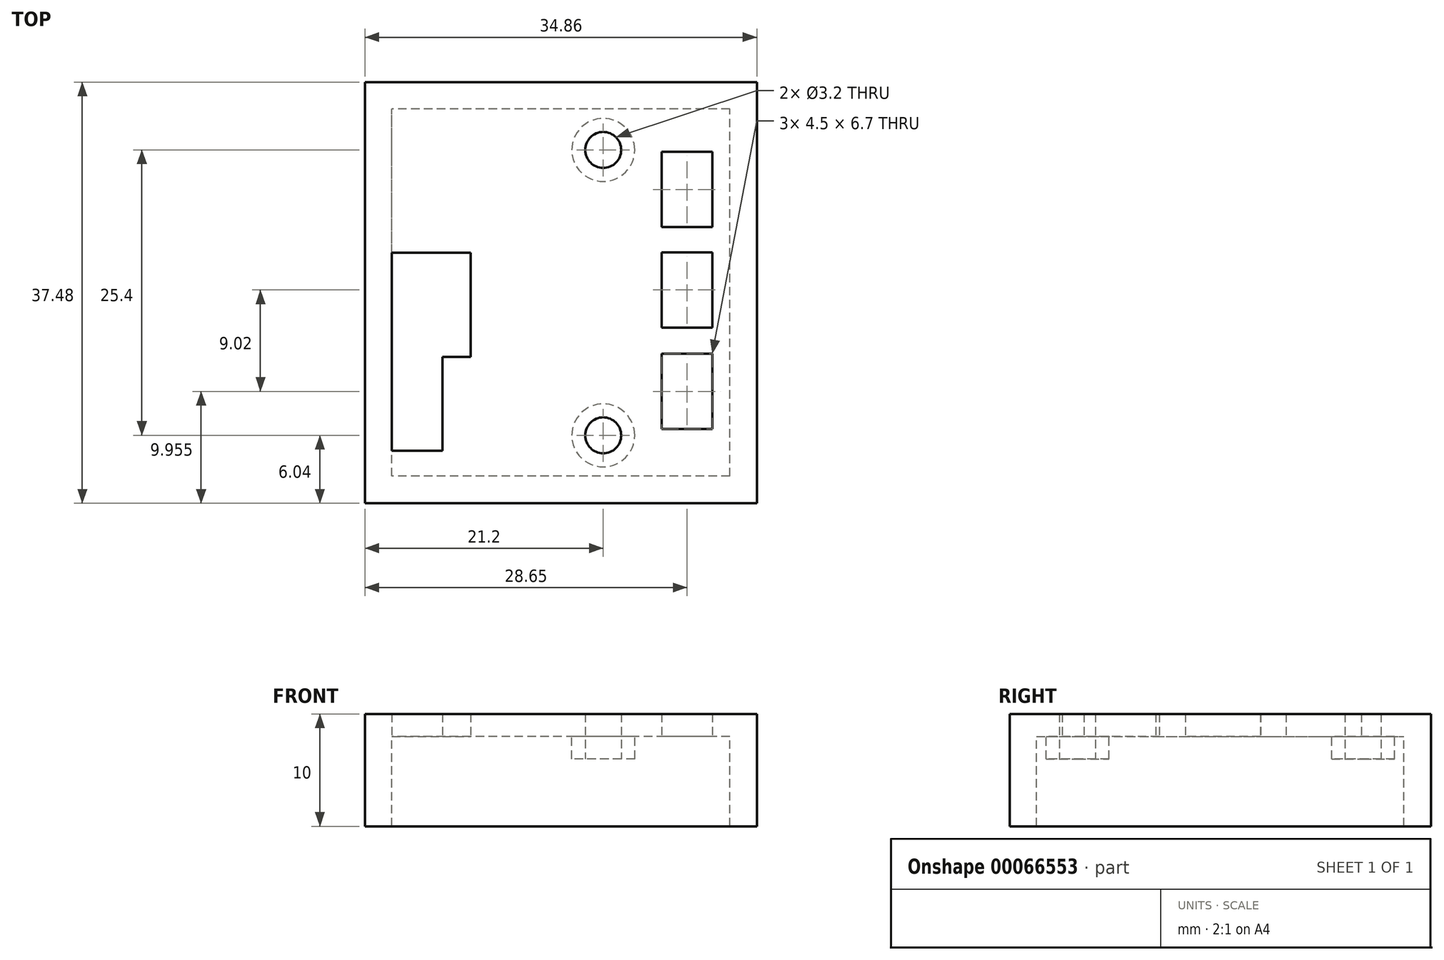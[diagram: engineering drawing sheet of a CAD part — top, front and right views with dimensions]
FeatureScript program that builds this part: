
annotation { "Feature Type Name" : "Feature", "Feature Type Description" : "" }
export const myFeature = defineFeature(function(context is Context, id is Id, definition is map)
    precondition{}
    {
        {
            var Q0;
            Q0=qCreatedBy(makeId("Top.planeOp"),FACE);
            var sketch = newSketch(context, id + "F0", { "sketchPlane" : qUnion([Q0])});
            skLineSegment(sketch, "E0.rect.bottom", {"start": v(14.03, -15.33) * mm, "end": v(-14.03, -15.34) * mm, "construction": true});
            skLineSegment(sketch, "E0.rect.top", {"start": v(14.03, 15.33) * mm, "end": v(-14.03, 15.33) * mm, "construction": true});
            skLineSegment(sketch, "E0.rect.left", {"start": v(14.03, -15.33) * mm, "end": v(14.03, 15.34) * mm, "construction": true});
            skLineSegment(sketch, "E0.rect.right", {"start": v(-14.03, -15.34) * mm, "end": v(-14.03, 15.34) * mm, "construction": true});
            skPoint(sketch, "E0.rect.middle", {"position": v(0, 0) * mm});
            skCircle(sketch, "E1", {"center": v(3.77, 12.7) * mm, "radius": 1.6 * mm});
            skCircle(sketch, "E2", {"center": v(3.77, -12.7) * mm, "radius": 1.6 * mm});
            skPoint(sketch, "E3", {"position": v(3.77, 14.3) * mm});
            skPoint(sketch, "E4", {"position": v(3.77, -11.1) * mm});
            skPoint(sketch, "E5", {"position": v(3.77, -14.3) * mm});
            skPoint(sketch, "E6", {"position": v(3.77, 11.1) * mm});
            skLineSegment(sketch, "E7.rect.bottom", {"start": v(15.03, -16.33) * mm, "end": v(-15.03, -16.34) * mm});
            skLineSegment(sketch, "E7.rect.top", {"start": v(15.03, 16.34) * mm, "end": v(-15.03, 16.33) * mm});
            skLineSegment(sketch, "E7.rect.left", {"start": v(15.03, -16.33) * mm, "end": v(15.03, 16.34) * mm});
            skLineSegment(sketch, "E7.rect.right", {"start": v(-15.03, -16.34) * mm, "end": v(-15.03, 16.33) * mm});
            skLineSegment(sketch, "E8.rect.bottom", {"start": v(17.43, -18.73) * mm, "end": v(-17.43, -18.74) * mm});
            skLineSegment(sketch, "E8.rect.top", {"start": v(17.43, 18.74) * mm, "end": v(-17.43, 18.73) * mm});
            skLineSegment(sketch, "E8.rect.left", {"start": v(17.43, -18.73) * mm, "end": v(17.43, 18.74) * mm});
            skLineSegment(sketch, "E8.rect.right", {"start": v(-17.43, -18.74) * mm, "end": v(-17.43, 18.73) * mm});
            skCircle(sketch, "E9", {"center": v(3.77, 12.7) * mm, "radius": 2.8 * mm});
            skCircle(sketch, "E10", {"center": v(3.77, -12.7) * mm, "radius": 2.8 * mm});
            skLineSegment(sketch, "E11.rect.bottom", {"start": v(12.47, 6.84) * mm, "end": v(9.97, 6.84) * mm, "construction": true});
            skLineSegment(sketch, "E11.rect.top", {"start": v(12.47, 11.54) * mm, "end": v(9.97, 11.54) * mm, "construction": true});
            skLineSegment(sketch, "E11.rect.left", {"start": v(12.47, 6.84) * mm, "end": v(12.47, 11.54) * mm, "construction": true});
            skLineSegment(sketch, "E11.rect.right", {"start": v(9.97, 6.84) * mm, "end": v(9.97, 11.54) * mm, "construction": true});
            skPoint(sketch, "E11.rect.middle", {"position": v(11.22, 9.19) * mm});
            skLineSegment(sketch, "E12.rect.bottom", {"start": v(12.47, -2.12) * mm, "end": v(9.97, -2.12) * mm, "construction": true});
            skLineSegment(sketch, "E12.rect.top", {"start": v(12.47, 2.58) * mm, "end": v(9.97, 2.58) * mm, "construction": true});
            skLineSegment(sketch, "E12.rect.left", {"start": v(12.47, -2.12) * mm, "end": v(12.47, 2.59) * mm, "construction": true});
            skLineSegment(sketch, "E12.rect.right", {"start": v(9.97, -2.12) * mm, "end": v(9.97, 2.59) * mm, "construction": true});
            skPoint(sketch, "E12.rect.middle", {"position": v(11.22, 0.24) * mm});
            skLineSegment(sketch, "E13.rect.bottom", {"start": v(12.47, -6.43) * mm, "end": v(9.97, -6.43) * mm, "construction": true});
            skLineSegment(sketch, "E13.rect.top", {"start": v(12.47, -11.13) * mm, "end": v(9.97, -11.13) * mm, "construction": true});
            skLineSegment(sketch, "E13.rect.left", {"start": v(12.47, -6.43) * mm, "end": v(12.47, -11.13) * mm, "construction": true});
            skLineSegment(sketch, "E13.rect.right", {"start": v(9.97, -6.43) * mm, "end": v(9.97, -11.13) * mm, "construction": true});
            skPoint(sketch, "E13.rect.middle", {"position": v(11.22, -8.79) * mm});
            skPoint(sketch, "E13.rect.middle.positionSnap0", {"position": v(11.22, -2.12) * mm});
            skPoint(sketch, "E13.rect.centerSnap0", {"position": v(11.22, -2.12) * mm});
            skLineSegment(sketch, "E14.rect.bottom", {"start": v(13.47, 5.84) * mm, "end": v(8.97, 5.84) * mm});
            skLineSegment(sketch, "E14.rect.top", {"start": v(13.47, 12.54) * mm, "end": v(8.97, 12.54) * mm});
            skLineSegment(sketch, "E14.rect.left", {"start": v(13.47, 5.84) * mm, "end": v(13.47, 12.54) * mm});
            skLineSegment(sketch, "E14.rect.right", {"start": v(8.97, 5.83) * mm, "end": v(8.97, 12.54) * mm});
            skLineSegment(sketch, "E15.rect.bottom", {"start": v(13.47, 3.59) * mm, "end": v(8.97, 3.59) * mm});
            skLineSegment(sketch, "E15.rect.top", {"start": v(13.47, -3.12) * mm, "end": v(8.97, -3.12) * mm});
            skLineSegment(sketch, "E15.rect.left", {"start": v(13.47, 3.59) * mm, "end": v(13.47, -3.12) * mm});
            skLineSegment(sketch, "E15.rect.right", {"start": v(8.97, 3.59) * mm, "end": v(8.97, -3.12) * mm});
            skLineSegment(sketch, "E16.rect.bottom", {"start": v(13.47, -5.43) * mm, "end": v(8.97, -5.43) * mm});
            skLineSegment(sketch, "E16.rect.top", {"start": v(13.47, -12.13) * mm, "end": v(8.97, -12.13) * mm});
            skLineSegment(sketch, "E16.rect.left", {"start": v(13.47, -5.43) * mm, "end": v(13.47, -12.13) * mm});
            skLineSegment(sketch, "E16.rect.right", {"start": v(8.97, -5.43) * mm, "end": v(8.97, -12.13) * mm});
            skLineSegment(sketch, "E17.rect.bottom", {"start": v(-11.53, -13.06) * mm, "end": v(-14.03, -13.06) * mm, "construction": true});
            skLineSegment(sketch, "E17.rect.top", {"start": v(-11.53, -5.74) * mm, "end": v(-14.03, -5.74) * mm, "construction": true});
            skLineSegment(sketch, "E17.rect.left", {"start": v(-11.53, -13.06) * mm, "end": v(-11.53, -5.74) * mm, "construction": true});
            skLineSegment(sketch, "E17.rect.right", {"start": v(-14.03, -13.06) * mm, "end": v(-14.03, -5.74) * mm, "construction": true});
            skPoint(sketch, "E17.rect.middle", {"position": v(-12.78, -9.4) * mm});
            skLineSegment(sketch, "E18.rect.bottom", {"start": v(-9.03, -4.74) * mm, "end": v(-14.03, -4.74) * mm, "construction": true});
            skLineSegment(sketch, "E18.rect.top", {"start": v(-9.03, 2.56) * mm, "end": v(-14.03, 2.56) * mm, "construction": true});
            skLineSegment(sketch, "E18.rect.left", {"start": v(-9.03, -4.74) * mm, "end": v(-9.03, 2.56) * mm, "construction": true});
            skLineSegment(sketch, "E18.rect.right", {"start": v(-14.03, -4.74) * mm, "end": v(-14.03, 2.56) * mm, "construction": true});
            skPoint(sketch, "E18.rect.middle", {"position": v(-11.53, -1.09) * mm});
            skLineSegment(sketch, "E19", {"start": v(-14.03, -14.06) * mm, "end": v(-10.53, -14.06) * mm});
            skLineSegment(sketch, "E20", {"start": v(-10.53, -14.06) * mm, "end": v(-10.53, -5.74) * mm});
            skLineSegment(sketch, "E21", {"start": v(-10.53, -5.74) * mm, "end": v(-8.03, -5.74) * mm});
            skLineSegment(sketch, "E22", {"start": v(-8.03, -5.74) * mm, "end": v(-8.03, 3.56) * mm});
            skLineSegment(sketch, "E23", {"start": v(-8.03, 3.56) * mm, "end": v(-15.03, 3.56) * mm});
            skLineSegment(sketch, "E24", {"start": v(-15.03, 3.56) * mm, "end": v(-15.03, -14.06) * mm});
            skLineSegment(sketch, "E25", {"start": v(-15.03, -14.06) * mm, "end": v(-14.03, -14.06) * mm});
            skSolve(sketch);
        }
        {
            var Q0;
            {var subQ2=sQuery(id+"F0.wireOp",EDGE,"E7.rect.bottom");Q0=makeQuery(id+"F0.imprint","IMPRINT",FACE,{"disambiguationData":[TD([[makeQuery(id+"F0.imprint","IMPRINT",EDGE,{"derivedFrom":subQ2}),-1.0]])]});}
            var Q1;
            {var subQ1=sQuery(id+"F0.wireOp",EDGE,"E7.rect.bottom");Q1=makeQuery(id+"F0.imprint","IMPRINT",FACE,{"disambiguationData":[TD([[makeQuery(id+"F0.imprint","IMPRINT",EDGE,{"derivedFrom":subQ1}),1.0]])]});}
            var Q2;
            Q2=makeQuery(id+"F0.imprint","IMPRINT",FACE,{"disambiguationData":[TD([[makeQuery(id+"F0.imprint","IMPRINT",EDGE,{"derivedFrom":sQuery(id+"F0.wireOp",EDGE,"E1")}),-1.0]])]});
            var Q3;
            Q3=makeQuery(id+"F0.imprint","IMPRINT",FACE,{"disambiguationData":[TD([[makeQuery(id+"F0.imprint","IMPRINT",EDGE,{"derivedFrom":sQuery(id+"F0.wireOp",EDGE,"E2")}),-1.0]])]});
            extrude(context, id + "F1", {"entities" : qUnion([Q0, Q1, Q2, Q3]), "depth" : 2 * mm});
        }
        {
            var Q0;
            {var subQ1=sQuery(id+"F0.wireOp",EDGE,"E7.rect.bottom");Q0=makeQuery(id+"F0.imprint","IMPRINT",FACE,{"disambiguationData":[TD([[makeQuery(id+"F0.imprint","IMPRINT",EDGE,{"derivedFrom":subQ1}),1.0]])]});}
            extrude(context, id + "F2", {"entities" : qUnion([Q0]), "operationType" : NewBodyOperationType.ADD, "oppositeDirection" : true, "depth" : 8 * mm});
        }
        {
            var Q0;
            Q0=makeQuery(id+"F0.imprint","IMPRINT",FACE,{"disambiguationData":[TD([[makeQuery(id+"F0.imprint","IMPRINT",EDGE,{"derivedFrom":sQuery(id+"F0.wireOp",EDGE,"E1")}),-1.0]])]});
            var Q1;
            Q1=makeQuery(id+"F0.imprint","IMPRINT",FACE,{"disambiguationData":[TD([[makeQuery(id+"F0.imprint","IMPRINT",EDGE,{"derivedFrom":sQuery(id+"F0.wireOp",EDGE,"E2")}),-1.0]])]});
            extrude(context, id + "F3", {"entities" : qUnion([Q0, Q1]), "operationType" : NewBodyOperationType.ADD, "oppositeDirection" : true, "depth" : 2 * mm});
        }
    });
